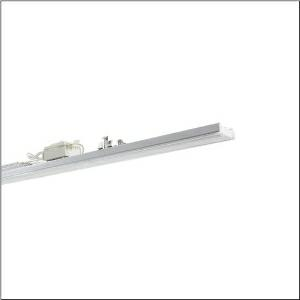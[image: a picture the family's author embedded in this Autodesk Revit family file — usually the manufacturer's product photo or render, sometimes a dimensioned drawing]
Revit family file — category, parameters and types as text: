
# Revit family: licross_r__21_recessed_mo_52tl1edn465g_00db
name_source: partatom
category: Lighting Fixtures
units: mm (PartAtom-declared; Revit-internal decimal feet)

## family parameters
Cut with Voids When Loaded = No
Host = Face
Light Source = No
Part Type = Normal
Room Calculation Point = No
Round Connector Dimension = Use Diameter
Shared = No

## types (1)
- --- (1 x LED, 6990 lm, 39.3 W, 4000K)
    Apparent Load = 39 VA
    CIE Flux Codes = 85 95 99 100 100
    Color Rendering = 80
    Color Temperature = 4000K
    Default Elevation = 1800 mm
    Description = Licross® 21 Recessed MO, luminaire insert, of sheet steel, galvanised, coil coated, white, length: 1.500mm, width: 66mm, height: 67mm, LED rated luminous flux: 6.990lm, light colour: 840, control gear: DALI 2, with plug, 5-pole, with phase selection, mains connection: 220..240V, AC, 50/60Hz, rated input power: 39W, internal wiring halogen-free, primary light control with lens, of plastic, primary optical cover: cover, of PMMA, light emission: direct distribution, primary light characteristic: symmetric, protection rating (complete): IP40, insulation class (complete): insulation class I (protective earthing), certification: CE, ENEC, VDE, UKCA, protection symbol: D if used in an environment without relevant dust loads with corresponding accessories, impact resistance: IK06, permissible ambient temperature for indoor applications: -25..+40°C, corresponds to IFS (International Featured Standards) requirements for safety and quality in the food industry, reducing of maximum allowable ambient temperature of 5°C with ceiling mounting, LABS conformity tested according to VDMA 24364:2018-05, packaging unit: 1 piece
    Height = 58 mm
    Lamp = 1 x LED
    Lamp Light Flux = 6990 lm
    Lamp Power = 39.3 W
    Lamp count = 1
    Length = 1500 mm
    Luminous efficacy = 178 lm/W
    Manufacturer = Siteco
    ModVariant = No
    Model = 52TL1EDN465G
    Mounting Place = Ceiling
    Mounting Type = Pendant
    Number of Poles = 1
    OnlyDefault = Yes
    Power Factor = 1
    Product Name = Licross® 21 Recessed MO
    Product group = luminaire insert | ceiling pendant
    ProductGroupID = 902
    Protection Class = Protection class I
    Protection Degree = IP 40
    RLX_Detail_Level = 1
    RLX_Emergency_Light_Flux = 0 lm
    RLX_Emergency_Type = 0
    RLX_Emergency_Type_DB = No
    RlxData = <blob elided: 24297 chars, md5=35fbfb0d>
    Socket = socket
    Standby Power = 0 W
    System Light Flux = 6990 lm
    System Power = 39 W
    Type Comments = factory setting: luminous flux: 100 % | dim-lin: 254 | 267 mA
    Type Image = l_1296930.jpg
    URL = http://relux.com
    VarID = @adj_146863
    Voltage = 0 V
    Weight = 0.00 kg
    Width = 66 mm

## geometry (parser evidence)
native form markers: Blend x4, Sweep x10
no freeform markers — native parametric forms only
